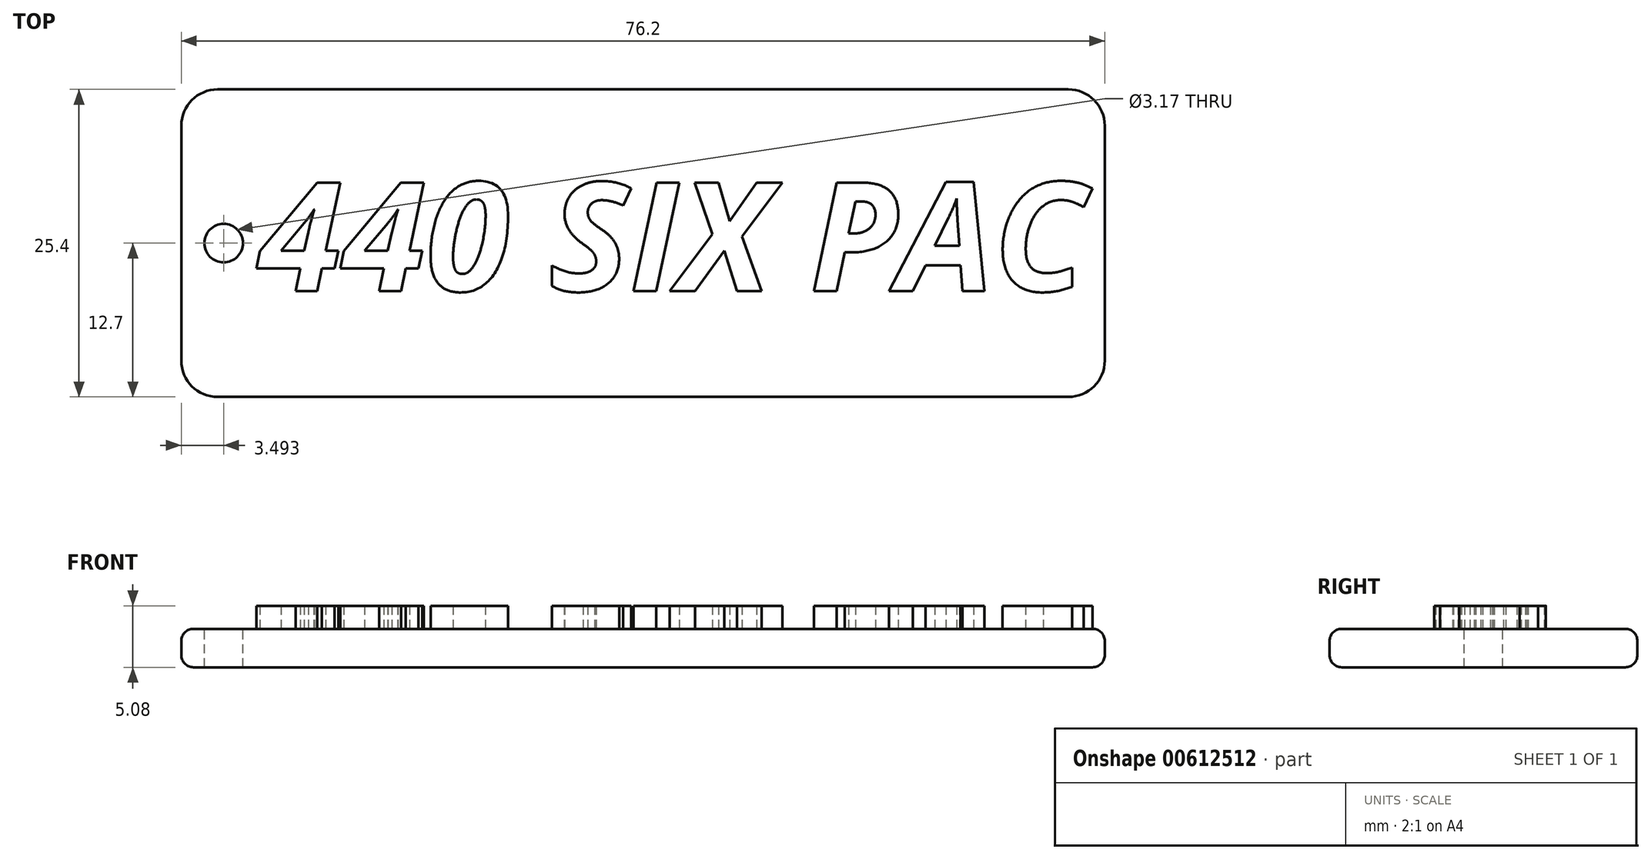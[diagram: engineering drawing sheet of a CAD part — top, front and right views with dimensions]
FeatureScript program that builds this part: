
annotation { "Feature Type Name" : "Feature", "Feature Type Description" : "" }
export const myFeature = defineFeature(function(context is Context, id is Id, definition is map)
    precondition{}
    {
        {
            var Q0;
            Q0=qCreatedBy(makeId("Top.planeOp"),FACE);
            var sketch = newSketch(context, id + "F0", { "sketchPlane" : qUnion([Q0])});
            skLineSegment(sketch, "E0.bottom", {"start": v(-3, 0) * mm, "end": v(-73.2, 0) * mm});
            skLineSegment(sketch, "E0.top", {"start": v(-3, 25.4) * mm, "end": v(-73.2, 25.4) * mm});
            skLineSegment(sketch, "E0.left", {"start": v(0, 3) * mm, "end": v(0, 22.4) * mm});
            skLineSegment(sketch, "E0.right", {"start": v(-76.2, 3) * mm, "end": v(-76.2, 22.4) * mm});
            skPoint(sketch, "E1.visualSharp", {"position": v(0, 25.4) * mm});
            skArc(sketch, "E1.filletArc", {"start": v(0, 22.4) * mm, "mid": v(-0.88, 24.52) * mm, "end": v(-3, 25.4) * mm});
            skPoint(sketch, "E2.visualSharp", {"position": v(0, 0) * mm});
            skArc(sketch, "E2.filletArc", {"start": v(-3, 0) * mm, "mid": v(-0.88, 0.88) * mm, "end": v(0, 3) * mm});
            skPoint(sketch, "E3.visualSharp", {"position": v(-76.2, 25.4) * mm});
            skArc(sketch, "E3.filletArc", {"start": v(-73.2, 25.4) * mm, "mid": v(-75.32, 24.52) * mm, "end": v(-76.2, 22.4) * mm});
            skPoint(sketch, "E4.visualSharp", {"position": v(-76.2, 0) * mm});
            skArc(sketch, "E4.filletArc", {"start": v(-76.2, 3) * mm, "mid": v(-75.32, 0.88) * mm, "end": v(-73.2, 0) * mm});
            skSolve(sketch);
        }
        {
            var Q0;
            Q0=makeQuery(id+"F0.imprint","IMPRINT",FACE,{"disambiguationData":[TD([[makeQuery(id+"F0.imprint","IMPRINT",EDGE,{"derivedFrom":sQuery(id+"F0.wireOp",EDGE,"E0.bottom")}),-1.0]])]});
            var sketch = newSketch(context, id + "F1", { "sketchPlane" : qUnion([Q0])});
            skText(sketch, "E5", { "text": "440 SIX PAC ", "fontName": "OpenSans-BoldItalic.ttf"});
            const initialGuessF1  = {"E5": [-0.06985, 0.00875, 1, 0, 0.00903]};
            skSetInitialGuess(sketch, initialGuessF1);
            skSolve(sketch);
        }
        {
            var Q0;
            Q0 = qSketchRegion(id + "F0", true);
            extrude(context, id + "F2", {"entities" : qUnion([Q0]), "depth" : 3.17 * mm, "offsetDistance" : 25.4 * mm});
        }
        {
            var Q0;
            Q0 = qSketchRegion(id + "F1", true);
            extrude(context, id + "F3", {"entities" : qUnion([Q0]), "operationType" : NewBodyOperationType.ADD, "depth" : 5.08 * mm, "offsetDistance" : 25.4 * mm});
        }
        {
            var Q0;
            {var subQ0=sQuery(id+"F0.wireOp",EDGE,"E0.top");var subQ1=sQuery(id+"F0.wireOp",EDGE,"E0.left");var subQ2=sQuery(id+"F0.wireOp",EDGE,"E0.right");var subQ3=sQuery(id+"F0.wireOp",EDGE,"E0.bottom");Q0=makeQuery(id+"F3.boolean.opBoolean","SPLIT",FACE,{"disambiguationData":[TD([makeQuery(id+"F2.opExtrude","SWEPT_FACE",FACE,{"disambiguationData":[OSD([subQ3])]})])],"derivedFrom":makeQuery(id+"F2.opExtrude","CAP_FACE",FACE,{"disambiguationData":[OSD([subQ3,subQ0,subQ1,subQ2])],"isStart":false})});}
            var sketch = newSketch(context, id + "F4", { "sketchPlane" : qUnion([Q0])});
            skCircle(sketch, "E6", {"center": v(-72.7, 12.7) * mm, "radius": 1.59 * mm});
            skSolve(sketch);
        }
        {
            var Q0;
            Q0=makeQuery(id+"F4.imprint","IMPRINT",FACE,{"disambiguationData":[TD([[makeQuery(id+"F4.imprint","IMPRINT",EDGE,{"derivedFrom":sQuery(id+"F4.wireOp",EDGE,"E6")}),1.0]])]});
            extrude(context, id + "F5", {"entities" : qUnion([Q0]), "operationType" : NewBodyOperationType.REMOVE, "endBound" : BoundingType.THROUGH_ALL, "oppositeDirection" : true, "depth" : 3.17 * mm, "offsetDistance" : 25.4 * mm});
        }
        {
            var Q0;
            Q0=makeQuery(id+"F2.opExtrude","CAP_EDGE",EDGE,{"disambiguationData":[OSD([sQuery(id+"F0.wireOp",EDGE,"E0.bottom")])],"isStart":false});
            fillet(context, id + "F6", {"entities" : qUnion([Q0]), "radius" : 1 * mm, "tangentPropagation" : true, "allowEdgeOverflow" : false});
        }
        {
            var Q0;
            Q0=makeQuery(id+"F2.opExtrude","CAP_EDGE",EDGE,{"disambiguationData":[OSD([sQuery(id+"F0.wireOp",EDGE,"E0.bottom")])],"isStart":true});
            fillet(context, id + "F7", {"entities" : qUnion([Q0]), "radius" : 1 * mm, "tangentPropagation" : true, "allowEdgeOverflow" : false});
        }
    });
